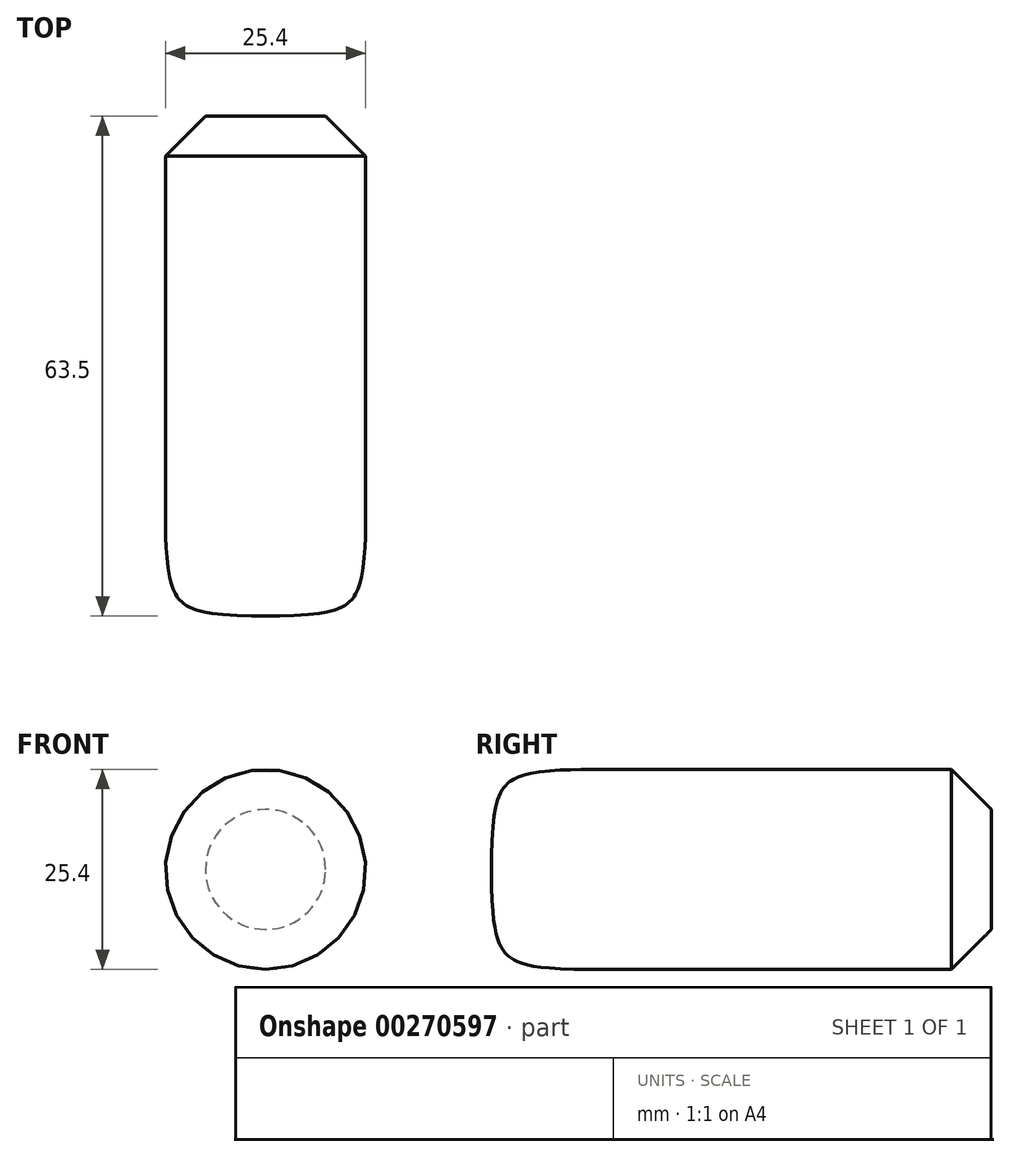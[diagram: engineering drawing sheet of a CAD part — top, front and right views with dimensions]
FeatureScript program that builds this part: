
annotation { "Feature Type Name" : "Feature", "Feature Type Description" : "" }
export const myFeature = defineFeature(function(context is Context, id is Id, definition is map)
    precondition{}
    {
        {
            var Q0;
            Q0=qCreatedBy(makeId("Front.planeOp"),FACE);
            var sketch = newSketch(context, id + "F0", { "sketchPlane" : qUnion([Q0])});
            skCircle(sketch, "E0", {"center": v(0, 0) * mm, "radius": 12.7 * mm});
            skSolve(sketch);
        }
        {
            var Q0;
            Q0 = qSketchRegion(id + "F0", true);
            extrude(context, id + "F1", {"entities" : qUnion([Q0]), "depth" : 63.5 * mm});
        }
        {
            var Q0;
            Q0=makeQuery(id+"F1.opExtrude","CAP_FACE",FACE,{"disambiguationData":[OSD([sQuery(id+"F0.wireOp",EDGE,"E0")])],"isStart":true});
            chamfer(context, id + "F2", {"entities" : qUnion([Q0]), "width" : 5.08 * mm, "tangentPropagation" : true});
        }
        {
            var Q0;
            Q0=makeQuery(id+"F1.opExtrude","CAP_FACE",FACE,{"disambiguationData":[OSD([sQuery(id+"F0.wireOp",EDGE,"E0")])],"isStart":false});
            fillet(context, id + "F3", {"entities" : qUnion([Q0]), "radius" : 12.7 * mm, "tangentPropagation" : true, "rho" : 0.7, "crossSection" : FilletCrossSection.CONIC, "allowEdgeOverflow" : false});
        }
    });
